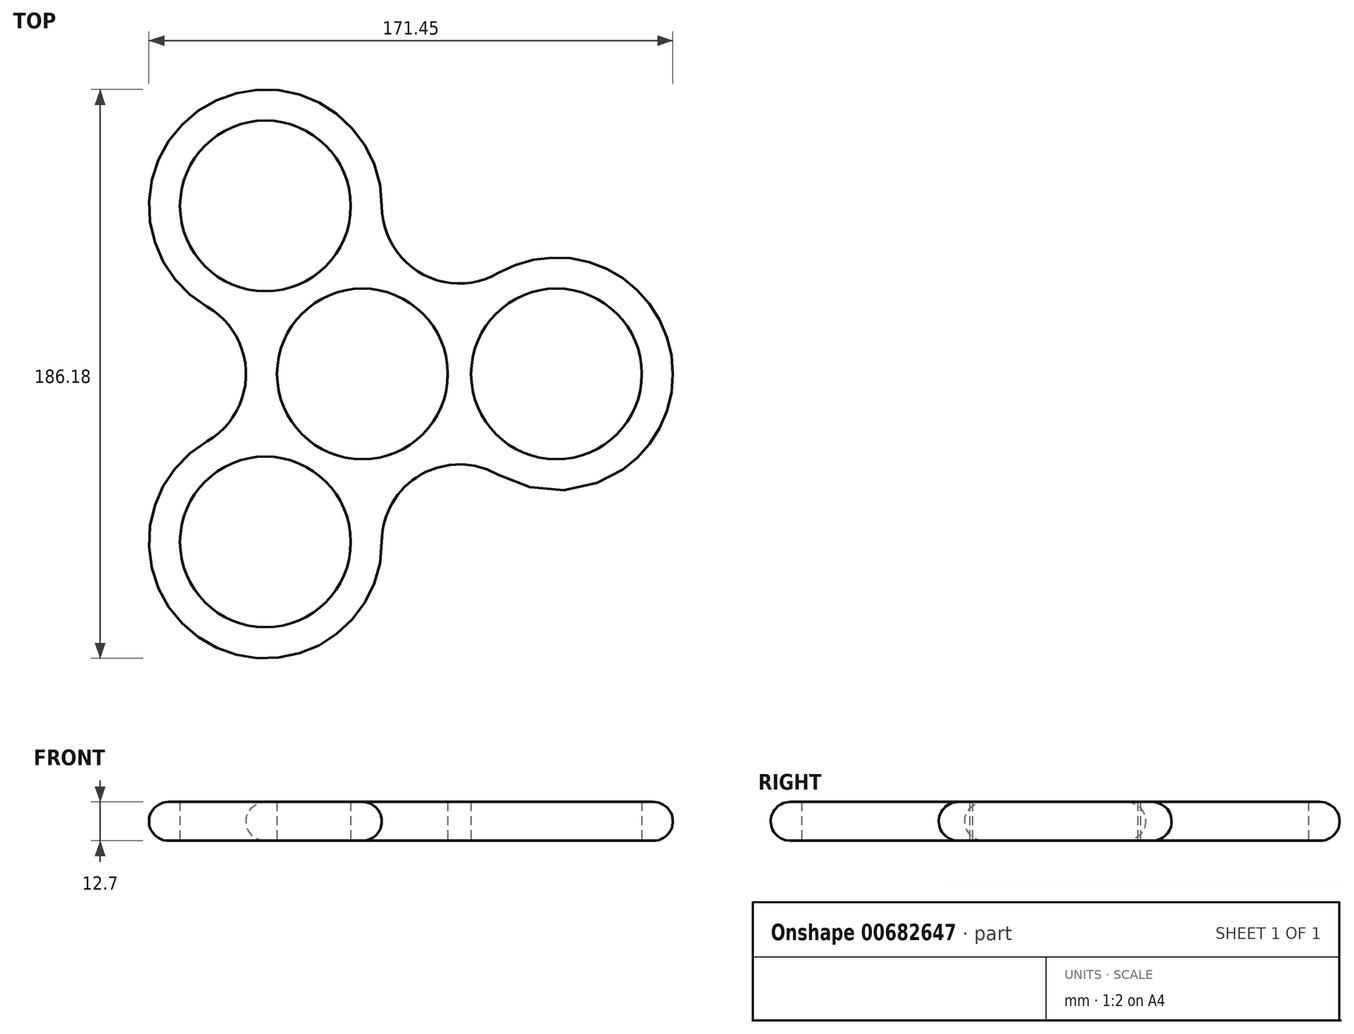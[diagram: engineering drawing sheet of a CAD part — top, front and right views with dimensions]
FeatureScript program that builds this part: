
annotation { "Feature Type Name" : "Feature", "Feature Type Description" : "" }
export const myFeature = defineFeature(function(context is Context, id is Id, definition is map)
    precondition{}
    {
        {
            var Q0;
            Q0=qCreatedBy(makeId("Top.planeOp"),FACE);
            var sketch = newSketch(context, id + "F0", { "sketchPlane" : qUnion([Q0])});
            skCircle(sketch, "E0", {"center": v(0, 0) * mm, "radius": 27.94 * mm});
            skCircle(sketch, "E1", {"center": v(0, 0) * mm, "radius": 38.1 * mm});
            skCircle(sketch, "E2.1.0.0", {"center": v(63.5, 0) * mm, "radius": 38.1 * mm});
            skCircle(sketch, "E2.1.0.1", {"center": v(63.5, 0) * mm, "radius": 27.94 * mm});
            skLineSegment(sketch, "E2.direction1", {"start": v(0, 0) * mm, "end": v(63.5, 0) * mm, "construction": true});
            skCircle(sketch, "E3.1.0", {"center": v(-31.75, 55) * mm, "radius": 38.1 * mm});
            skCircle(sketch, "E3.1.1", {"center": v(-31.75, 55) * mm, "radius": 27.94 * mm});
            skCircle(sketch, "E3.2.0", {"center": v(-31.75, -55) * mm, "radius": 38.1 * mm});
            skCircle(sketch, "E3.2.1", {"center": v(-31.75, -55) * mm, "radius": 27.94 * mm});
            skSolve(sketch);
        }
        {
            var Q0;
            {var subQ0=sQuery(id+"F0.wireOp",EDGE,"E3.1.0");var subQ1=sQuery(id+"F0.wireOp",EDGE,"E1");var subQ2=makeQuery(id+"F0.imprint","INTERSECT",VERTEX,{"disambiguationData":[OD(0.0)],"derivedFrom":[subQ1,subQ0]});Q0=makeQuery(id+"F0.imprint","IMPRINT",FACE,{"disambiguationData":[TD([[makeQuery(id+"F0.imprint","IMPRINT",EDGE,{"disambiguationData":[TD([[subQ2,-1.0]])],"derivedFrom":subQ1}),-1.0]])]});}
            var Q1;
            {var subQ0=sQuery(id+"F0.wireOp",EDGE,"E3.1.0");var subQ1=sQuery(id+"F0.wireOp",EDGE,"E0");var subQ2=makeQuery(id+"F0.imprint","INTERSECT",VERTEX,{"disambiguationData":[OD(1.0)],"derivedFrom":[subQ1,subQ0]});Q1=makeQuery(id+"F0.imprint","IMPRINT",FACE,{"disambiguationData":[TD([[makeQuery(id+"F0.imprint","IMPRINT",EDGE,{"disambiguationData":[TD([[subQ2,-1.0]])],"derivedFrom":subQ1}),-1.0]])]});}
            var Q2;
            {var subQ0=sQuery(id+"F0.wireOp",EDGE,"E3.2.0");var subQ1=sQuery(id+"F0.wireOp",EDGE,"E1");var subQ2=makeQuery(id+"F0.imprint","INTERSECT",VERTEX,{"disambiguationData":[OD(0.0)],"derivedFrom":[subQ1,subQ0]});Q2=makeQuery(id+"F0.imprint","IMPRINT",FACE,{"disambiguationData":[TD([[makeQuery(id+"F0.imprint","IMPRINT",EDGE,{"disambiguationData":[TD([[subQ2,-1.0]])],"derivedFrom":subQ1}),-1.0]])]});}
            var Q3;
            {var subQ0=sQuery(id+"F0.wireOp",EDGE,"E3.2.0");var subQ1=sQuery(id+"F0.wireOp",EDGE,"E0");var subQ2=makeQuery(id+"F0.imprint","INTERSECT",VERTEX,{"disambiguationData":[OD(1.0)],"derivedFrom":[subQ1,subQ0]});Q3=makeQuery(id+"F0.imprint","IMPRINT",FACE,{"disambiguationData":[TD([[makeQuery(id+"F0.imprint","IMPRINT",EDGE,{"disambiguationData":[TD([[subQ2,-1.0]])],"derivedFrom":subQ1}),-1.0]])]});}
            var Q4;
            {var subQ0=sQuery(id+"F0.wireOp",EDGE,"E3.2.0");var subQ3=sQuery(id+"F0.wireOp",EDGE,"E0");var subQ7=makeQuery(id+"F0.imprint","INTERSECT",VERTEX,{"disambiguationData":[OD(0.0)],"derivedFrom":[subQ3,subQ0]});Q4=makeQuery(id+"F0.imprint","IMPRINT",FACE,{"disambiguationData":[TD([[makeQuery(id+"F0.imprint","IMPRINT",EDGE,{"disambiguationData":[TD([[subQ7,-1.0]])],"derivedFrom":subQ3}),-1.0]])]});}
            var Q5;
            {var subQ0=sQuery(id+"F0.wireOp",EDGE,"E2.1.0.0");var subQ1=sQuery(id+"F0.wireOp",EDGE,"E1");var subQ2=makeQuery(id+"F0.imprint","INTERSECT",VERTEX,{"disambiguationData":[OD(0.0)],"derivedFrom":[subQ1,subQ0]});Q5=makeQuery(id+"F0.imprint","IMPRINT",FACE,{"disambiguationData":[TD([[makeQuery(id+"F0.imprint","IMPRINT",EDGE,{"disambiguationData":[TD([[subQ2,1.0]])],"derivedFrom":subQ1}),-1.0]])]});}
            var Q6;
            {var subQ0=sQuery(id+"F0.wireOp",EDGE,"E3.1.0");var subQ1=sQuery(id+"F0.wireOp",EDGE,"E0");var subQ2=makeQuery(id+"F0.imprint","INTERSECT",VERTEX,{"disambiguationData":[OD(0.0)],"derivedFrom":[subQ1,subQ0]});Q6=makeQuery(id+"F0.imprint","IMPRINT",FACE,{"disambiguationData":[TD([[makeQuery(id+"F0.imprint","IMPRINT",EDGE,{"disambiguationData":[TD([[subQ2,1.0]])],"derivedFrom":subQ1}),-1.0]])]});}
            var Q7;
            {var subQ0=sQuery(id+"F0.wireOp",EDGE,"E2.1.0.0");var subQ3=sQuery(id+"F0.wireOp",EDGE,"E0");var subQ4=makeQuery(id+"F0.imprint","INTERSECT",VERTEX,{"disambiguationData":[OD(0.0)],"derivedFrom":[subQ3,subQ0]});Q7=makeQuery(id+"F0.imprint","IMPRINT",FACE,{"disambiguationData":[TD([[makeQuery(id+"F0.imprint","IMPRINT",EDGE,{"disambiguationData":[TD([[subQ4,1.0]])],"derivedFrom":subQ3}),-1.0]])]});}
            var Q8;
            {var subQ0=sQuery(id+"F0.wireOp",EDGE,"E3.1.0");var subQ3=sQuery(id+"F0.wireOp",EDGE,"E0");var subQ9=makeQuery(id+"F0.imprint","INTERSECT",VERTEX,{"disambiguationData":[OD(0.0)],"derivedFrom":[subQ3,subQ0]});Q8=makeQuery(id+"F0.imprint","IMPRINT",FACE,{"disambiguationData":[TD([[makeQuery(id+"F0.imprint","IMPRINT",EDGE,{"disambiguationData":[TD([[subQ9,-1.0]])],"derivedFrom":subQ3}),-1.0]])]});}
            extrude(context, id + "F1", {"entities" : qUnion([Q0, Q1, Q2, Q3, Q4, Q5, Q6, Q7, Q8]), "depth" : 12.7 * mm, "offsetDistance" : 25.4 * mm});
        }
        {
            var Q0;
            {var subQ0=sQuery(id+"F0.wireOp",EDGE,"E3.1.0");var subQ1=sQuery(id+"F0.wireOp",EDGE,"E1");Q0=makeQuery(id+"F1.opExtrude","SWEPT_EDGE",EDGE,{"disambiguationData":[OSD([subQ1,subQ0]),TDD([makeQuery(id+"F0.imprint","INTERSECT",VERTEX,{"disambiguationData":[OD(0.0)],"derivedFrom":[subQ1,subQ0]})])]});}
            var Q1;
            {var subQ0=sQuery(id+"F0.wireOp",EDGE,"E3.1.0");var subQ1=sQuery(id+"F0.wireOp",EDGE,"E1");Q1=makeQuery(id+"F1.opExtrude","SWEPT_EDGE",EDGE,{"disambiguationData":[OSD([subQ1,subQ0]),TDD([makeQuery(id+"F0.imprint","INTERSECT",VERTEX,{"disambiguationData":[OD(1.0)],"derivedFrom":[subQ1,subQ0]})])]});}
            var Q2;
            {var subQ0=sQuery(id+"F0.wireOp",EDGE,"E3.2.0");var subQ1=sQuery(id+"F0.wireOp",EDGE,"E1");Q2=makeQuery(id+"F1.opExtrude","SWEPT_EDGE",EDGE,{"disambiguationData":[OSD([subQ1,subQ0]),TDD([makeQuery(id+"F0.imprint","INTERSECT",VERTEX,{"disambiguationData":[OD(0.0)],"derivedFrom":[subQ1,subQ0]})])]});}
            var Q3;
            {var subQ0=sQuery(id+"F0.wireOp",EDGE,"E2.1.0.0");var subQ1=sQuery(id+"F0.wireOp",EDGE,"E1");Q3=makeQuery(id+"F1.opExtrude","SWEPT_EDGE",EDGE,{"disambiguationData":[OSD([subQ1,subQ0]),TDD([makeQuery(id+"F0.imprint","INTERSECT",VERTEX,{"disambiguationData":[OD(0.0)],"derivedFrom":[subQ1,subQ0]})])]});}
            var Q4;
            {var subQ0=sQuery(id+"F0.wireOp",EDGE,"E2.1.0.0");var subQ1=sQuery(id+"F0.wireOp",EDGE,"E1");Q4=makeQuery(id+"F1.opExtrude","SWEPT_EDGE",EDGE,{"disambiguationData":[OSD([subQ1,subQ0]),TDD([makeQuery(id+"F0.imprint","INTERSECT",VERTEX,{"disambiguationData":[OD(1.0)],"derivedFrom":[subQ1,subQ0]})])]});}
            var Q5;
            {var subQ0=sQuery(id+"F0.wireOp",EDGE,"E3.2.0");var subQ1=sQuery(id+"F0.wireOp",EDGE,"E1");Q5=makeQuery(id+"F1.opExtrude","SWEPT_EDGE",EDGE,{"disambiguationData":[OSD([subQ1,subQ0]),TDD([makeQuery(id+"F0.imprint","INTERSECT",VERTEX,{"disambiguationData":[OD(1.0)],"derivedFrom":[subQ1,subQ0]})])]});}
            fillet(context, id + "F2", {"entities" : qUnion([Q0, Q1, Q2, Q3, Q4, Q5]), "radius" : 25.4 * mm, "tangentPropagation" : true, "allowEdgeOverflow" : false});
        }
        {
            var Q0;
            Q0=makeQuery(id+"F1.opExtrude","CAP_EDGE",EDGE,{"disambiguationData":[OSD([sQuery(id+"F0.wireOp",EDGE,"E3.1.0")])],"isStart":true});
            var Q1;
            Q1=makeQuery(id+"F1.opExtrude","CAP_EDGE",EDGE,{"disambiguationData":[OSD([sQuery(id+"F0.wireOp",EDGE,"E3.1.0")])],"isStart":false});
            fillet(context, id + "F3", {"entities" : qUnion([Q0, Q1]), "radius" : 6.35 * mm, "tangentPropagation" : true, "allowEdgeOverflow" : false});
        }
    });
